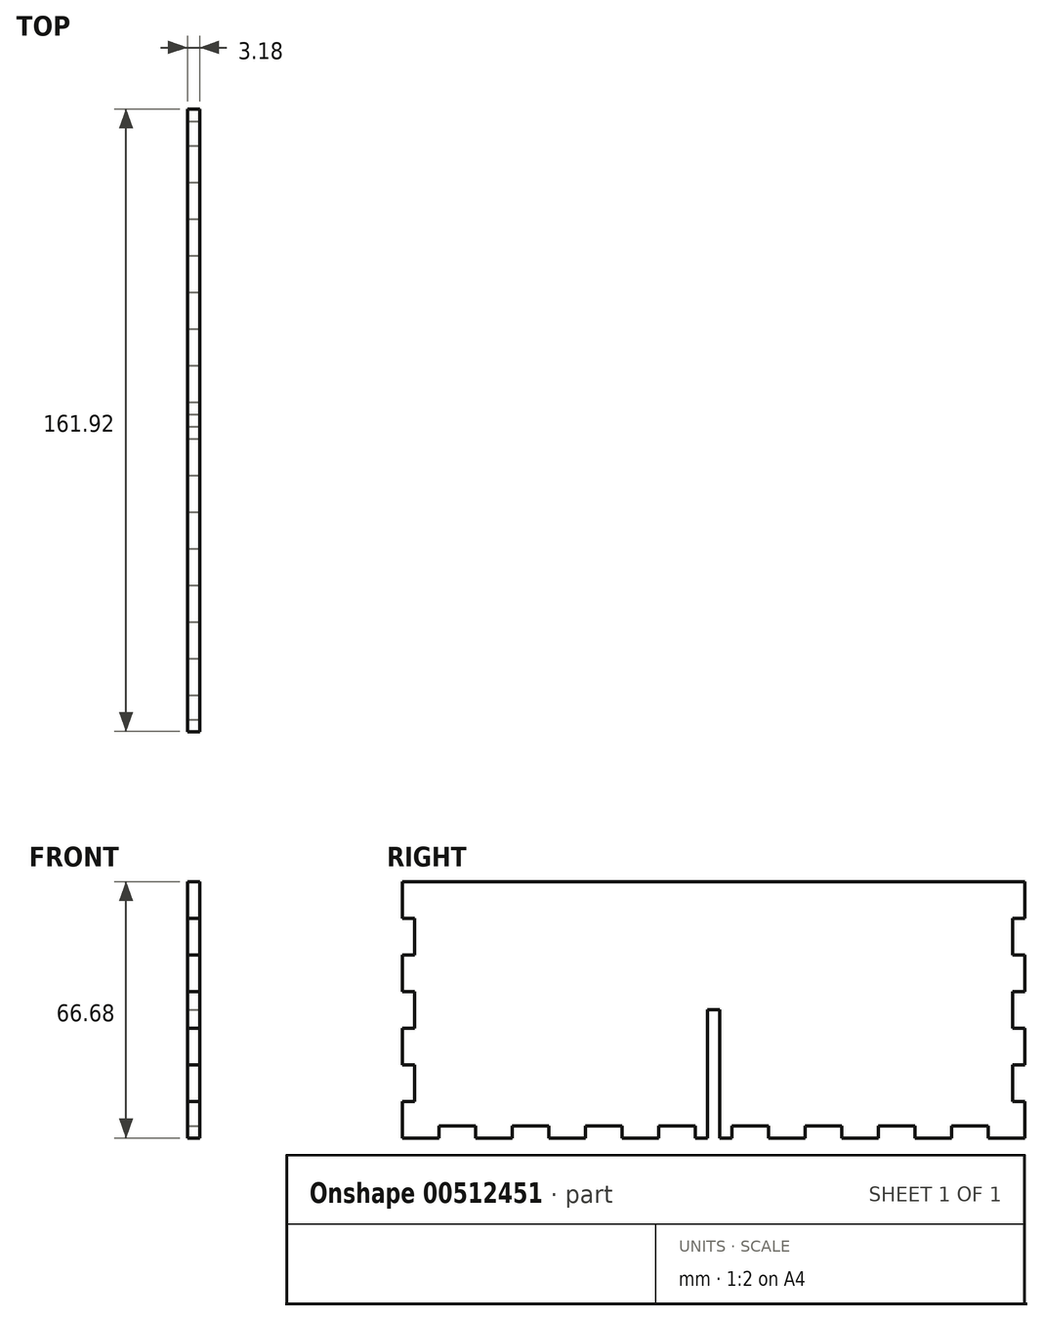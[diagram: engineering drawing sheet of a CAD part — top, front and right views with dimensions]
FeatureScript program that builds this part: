
annotation { "Feature Type Name" : "Feature", "Feature Type Description" : "" }
export const myFeature = defineFeature(function(context is Context, id is Id, definition is map)
    precondition{}
    {
        {
            var Q0;
            Q0=qCreatedBy(makeId("Right.planeOp"),FACE);
            var sketch = newSketch(context, id + "F0", { "sketchPlane" : qUnion([Q0])});
            skLineSegment(sketch, "E0.bottom", {"start": v(-80.96, 33.34) * mm, "end": v(80.96, 33.34) * mm});
            skLineSegment(sketch, "E0.top", {"start": v(-80.96, -33.34) * mm, "end": v(80.96, -33.34) * mm});
            skLineSegment(sketch, "E0.left", {"start": v(-80.96, 33.34) * mm, "end": v(-80.96, -33.34) * mm});
            skLineSegment(sketch, "E0.right", {"start": v(80.96, 33.34) * mm, "end": v(80.96, -33.34) * mm});
            skSolve(sketch);
        }
        {
            var Q0;
            Q0=makeQuery(id+"F0.imprint","IMPRINT",FACE,{"disambiguationData":[TD([[makeQuery(id+"F0.imprint","IMPRINT",EDGE,{"derivedFrom":sQuery(id+"F0.wireOp",EDGE,"E0.bottom")}),-1.0]])]});
            extrude(context, id + "F1", {"entities" : qUnion([Q0]), "depth" : 3.17 * mm});
        }
        {
            var Q0;
            Q0=makeQuery(id+"F1.opExtrude","CAP_FACE",FACE,{"disambiguationData":[OSD([sQuery(id+"F0.wireOp",EDGE,"E0.bottom"),sQuery(id+"F0.wireOp",EDGE,"E0.top"),sQuery(id+"F0.wireOp",EDGE,"E0.left"),sQuery(id+"F0.wireOp",EDGE,"E0.right")])],"isStart":false});
            var sketch = newSketch(context, id + "F2", { "sketchPlane" : qUnion([Q0])});
            skLineSegment(sketch, "E1.bottom", {"start": v(-80.96, -23.81) * mm, "end": v(-77.79, -23.81) * mm});
            skLineSegment(sketch, "E1.top", {"start": v(-80.96, -14.29) * mm, "end": v(-77.79, -14.29) * mm});
            skLineSegment(sketch, "E1.left", {"start": v(-80.96, -23.81) * mm, "end": v(-80.96, -14.29) * mm});
            skLineSegment(sketch, "E1.right", {"start": v(-77.79, -23.81) * mm, "end": v(-77.79, -14.29) * mm});
            skLineSegment(sketch, "E2.0.1.0", {"start": v(-77.79, -4.76) * mm, "end": v(-77.79, 4.76) * mm});
            skLineSegment(sketch, "E2.0.1.1", {"start": v(-80.96, -4.76) * mm, "end": v(-80.96, 4.76) * mm});
            skLineSegment(sketch, "E2.0.1.2", {"start": v(-80.96, -4.76) * mm, "end": v(-77.79, -4.76) * mm});
            skLineSegment(sketch, "E2.0.1.3", {"start": v(-80.96, 4.76) * mm, "end": v(-77.79, 4.76) * mm});
            skLineSegment(sketch, "E2.0.2.0", {"start": v(-77.79, 14.29) * mm, "end": v(-77.79, 23.81) * mm});
            skLineSegment(sketch, "E2.0.2.1", {"start": v(-80.96, 14.29) * mm, "end": v(-80.96, 23.81) * mm});
            skLineSegment(sketch, "E2.0.2.2", {"start": v(-80.96, 14.29) * mm, "end": v(-77.79, 14.29) * mm});
            skLineSegment(sketch, "E2.0.2.3", {"start": v(-80.96, 23.81) * mm, "end": v(-77.79, 23.81) * mm});
            skLineSegment(sketch, "E2.direction1", {"start": v(-80.96, -23.81) * mm, "end": v(77.79, -23.81) * mm, "construction": true});
            skLineSegment(sketch, "E2.direction2", {"start": v(-80.96, -23.81) * mm, "end": v(-80.96, -4.76) * mm, "construction": true});
            skLineSegment(sketch, "E3.0.1.0", {"start": v(80.96, -23.81) * mm, "end": v(80.96, -14.29) * mm});
            skLineSegment(sketch, "E3.3.1.0", {"start": v(77.79, -23.81) * mm, "end": v(77.79, -14.29) * mm});
            skLineSegment(sketch, "E3.6.1.0", {"start": v(77.79, -23.81) * mm, "end": v(80.96, -23.81) * mm});
            skLineSegment(sketch, "E3.9.1.0", {"start": v(77.79, -14.29) * mm, "end": v(80.96, -14.29) * mm});
            skLineSegment(sketch, "E3.0.1.1", {"start": v(80.96, -4.76) * mm, "end": v(80.96, 4.76) * mm});
            skLineSegment(sketch, "E3.3.1.1", {"start": v(77.79, -4.76) * mm, "end": v(77.79, 4.76) * mm});
            skLineSegment(sketch, "E3.6.1.1", {"start": v(77.79, -4.76) * mm, "end": v(80.96, -4.76) * mm});
            skLineSegment(sketch, "E3.9.1.1", {"start": v(77.79, 4.76) * mm, "end": v(80.96, 4.76) * mm});
            skLineSegment(sketch, "E3.0.1.2", {"start": v(80.96, 14.29) * mm, "end": v(80.96, 23.81) * mm});
            skLineSegment(sketch, "E3.3.1.2", {"start": v(77.79, 14.29) * mm, "end": v(77.79, 23.81) * mm});
            skLineSegment(sketch, "E3.6.1.2", {"start": v(77.79, 14.29) * mm, "end": v(80.96, 14.29) * mm});
            skLineSegment(sketch, "E3.9.1.2", {"start": v(77.79, 23.81) * mm, "end": v(80.96, 23.81) * mm});
            skSolve(sketch);
        }
        {
            var Q0;
            Q0=qSketchRegion(id+"F2",true);
            extrude(context, id + "F3", {"entities" : qUnion([Q0]), "operationType" : NewBodyOperationType.REMOVE, "endBound" : BoundingType.THROUGH_ALL, "oppositeDirection" : true, "depth" : 25.4 * mm});
        }
        {
            var Q0;
            Q0=makeQuery(id+"F1.opExtrude","CAP_FACE",FACE,{"disambiguationData":[OSD([sQuery(id+"F0.wireOp",EDGE,"E0.bottom"),sQuery(id+"F0.wireOp",EDGE,"E0.top"),sQuery(id+"F0.wireOp",EDGE,"E0.left"),sQuery(id+"F0.wireOp",EDGE,"E0.right")])],"isStart":false});
            var sketch = newSketch(context, id + "F4", { "sketchPlane" : qUnion([Q0])});
            skLineSegment(sketch, "E4.bottom", {"start": v(-71.44, -33.34) * mm, "end": v(-61.91, -33.34) * mm});
            skLineSegment(sketch, "E4.top", {"start": v(-71.44, -30.16) * mm, "end": v(-61.91, -30.16) * mm});
            skLineSegment(sketch, "E4.left", {"start": v(-71.44, -33.34) * mm, "end": v(-71.44, -30.16) * mm});
            skLineSegment(sketch, "E4.right", {"start": v(-61.91, -33.34) * mm, "end": v(-61.91, -30.16) * mm});
            skLineSegment(sketch, "E5.1.0.0", {"start": v(-42.86, -33.34) * mm, "end": v(-42.86, -30.16) * mm});
            skLineSegment(sketch, "E5.1.0.1", {"start": v(-52.39, -33.34) * mm, "end": v(-52.39, -30.16) * mm});
            skLineSegment(sketch, "E5.1.0.2", {"start": v(-52.39, -30.16) * mm, "end": v(-42.86, -30.16) * mm});
            skLineSegment(sketch, "E5.1.0.3", {"start": v(-52.39, -33.34) * mm, "end": v(-42.86, -33.34) * mm});
            skLineSegment(sketch, "E5.2.0.0", {"start": v(-23.81, -33.34) * mm, "end": v(-23.81, -30.16) * mm});
            skLineSegment(sketch, "E5.2.0.1", {"start": v(-33.34, -33.34) * mm, "end": v(-33.34, -30.16) * mm});
            skLineSegment(sketch, "E5.2.0.2", {"start": v(-33.34, -30.16) * mm, "end": v(-23.81, -30.16) * mm});
            skLineSegment(sketch, "E5.2.0.3", {"start": v(-33.34, -33.34) * mm, "end": v(-23.81, -33.34) * mm});
            skLineSegment(sketch, "E5.3.0.0", {"start": v(-4.76, -33.34) * mm, "end": v(-4.76, -30.16) * mm});
            skLineSegment(sketch, "E5.3.0.1", {"start": v(-14.29, -33.34) * mm, "end": v(-14.29, -30.16) * mm});
            skLineSegment(sketch, "E5.3.0.2", {"start": v(-14.29, -30.16) * mm, "end": v(-4.76, -30.16) * mm});
            skLineSegment(sketch, "E5.3.0.3", {"start": v(-14.29, -33.34) * mm, "end": v(-4.76, -33.34) * mm});
            skLineSegment(sketch, "E5.4.0.0", {"start": v(14.29, -33.34) * mm, "end": v(14.29, -30.16) * mm});
            skLineSegment(sketch, "E5.4.0.1", {"start": v(4.76, -33.34) * mm, "end": v(4.76, -30.16) * mm});
            skLineSegment(sketch, "E5.4.0.2", {"start": v(4.76, -30.16) * mm, "end": v(14.29, -30.16) * mm});
            skLineSegment(sketch, "E5.4.0.3", {"start": v(4.76, -33.34) * mm, "end": v(14.29, -33.34) * mm});
            skLineSegment(sketch, "E5.5.0.0", {"start": v(33.34, -33.34) * mm, "end": v(33.34, -30.16) * mm});
            skLineSegment(sketch, "E5.5.0.1", {"start": v(23.81, -33.34) * mm, "end": v(23.81, -30.16) * mm});
            skLineSegment(sketch, "E5.5.0.2", {"start": v(23.81, -30.16) * mm, "end": v(33.34, -30.16) * mm});
            skLineSegment(sketch, "E5.5.0.3", {"start": v(23.81, -33.34) * mm, "end": v(33.34, -33.34) * mm});
            skLineSegment(sketch, "E5.6.0.0", {"start": v(52.39, -33.34) * mm, "end": v(52.39, -30.16) * mm});
            skLineSegment(sketch, "E5.6.0.1", {"start": v(42.86, -33.34) * mm, "end": v(42.86, -30.16) * mm});
            skLineSegment(sketch, "E5.6.0.2", {"start": v(42.86, -30.16) * mm, "end": v(52.39, -30.16) * mm});
            skLineSegment(sketch, "E5.6.0.3", {"start": v(42.86, -33.34) * mm, "end": v(52.39, -33.34) * mm});
            skLineSegment(sketch, "E5.7.0.0", {"start": v(71.44, -33.34) * mm, "end": v(71.44, -30.16) * mm});
            skLineSegment(sketch, "E5.7.0.1", {"start": v(61.91, -33.34) * mm, "end": v(61.91, -30.16) * mm});
            skLineSegment(sketch, "E5.7.0.2", {"start": v(61.91, -30.16) * mm, "end": v(71.44, -30.16) * mm});
            skLineSegment(sketch, "E5.7.0.3", {"start": v(61.91, -33.34) * mm, "end": v(71.44, -33.34) * mm});
            skLineSegment(sketch, "E5.direction1", {"start": v(-71.44, -33.34) * mm, "end": v(-52.39, -33.34) * mm, "construction": true});
            skSolve(sketch);
        }
        {
            var Q0;
            Q0=qSketchRegion(id+"F4",true);
            extrude(context, id + "F5", {"entities" : qUnion([Q0]), "operationType" : NewBodyOperationType.REMOVE, "endBound" : BoundingType.THROUGH_ALL, "oppositeDirection" : true, "depth" : 25.4 * mm});
        }
        {
            var Q0;
            Q0=makeQuery(id+"F1.opExtrude","CAP_FACE",FACE,{"disambiguationData":[OSD([sQuery(id+"F0.wireOp",EDGE,"E0.bottom"),sQuery(id+"F0.wireOp",EDGE,"E0.top"),sQuery(id+"F0.wireOp",EDGE,"E0.left"),sQuery(id+"F0.wireOp",EDGE,"E0.right")])],"isStart":false});
            var sketch = newSketch(context, id + "F6", { "sketchPlane" : qUnion([Q0])});
            skLineSegment(sketch, "E6.bottom", {"start": v(-1.59, -33.34) * mm, "end": v(1.59, -33.34) * mm});
            skLineSegment(sketch, "E6.top", {"start": v(-1.59, 0) * mm, "end": v(1.59, 0) * mm});
            skLineSegment(sketch, "E6.left", {"start": v(-1.59, -33.34) * mm, "end": v(-1.59, 0) * mm});
            skLineSegment(sketch, "E6.right", {"start": v(1.59, -33.34) * mm, "end": v(1.59, 0) * mm});
            skSolve(sketch);
        }
        {
            var Q0;
            Q0 = qSketchRegion(id + "F6", true);
            extrude(context, id + "F7", {"entities" : qUnion([Q0]), "operationType" : NewBodyOperationType.REMOVE, "endBound" : BoundingType.THROUGH_ALL, "oppositeDirection" : true, "depth" : 25.4 * mm});
        }
    });
